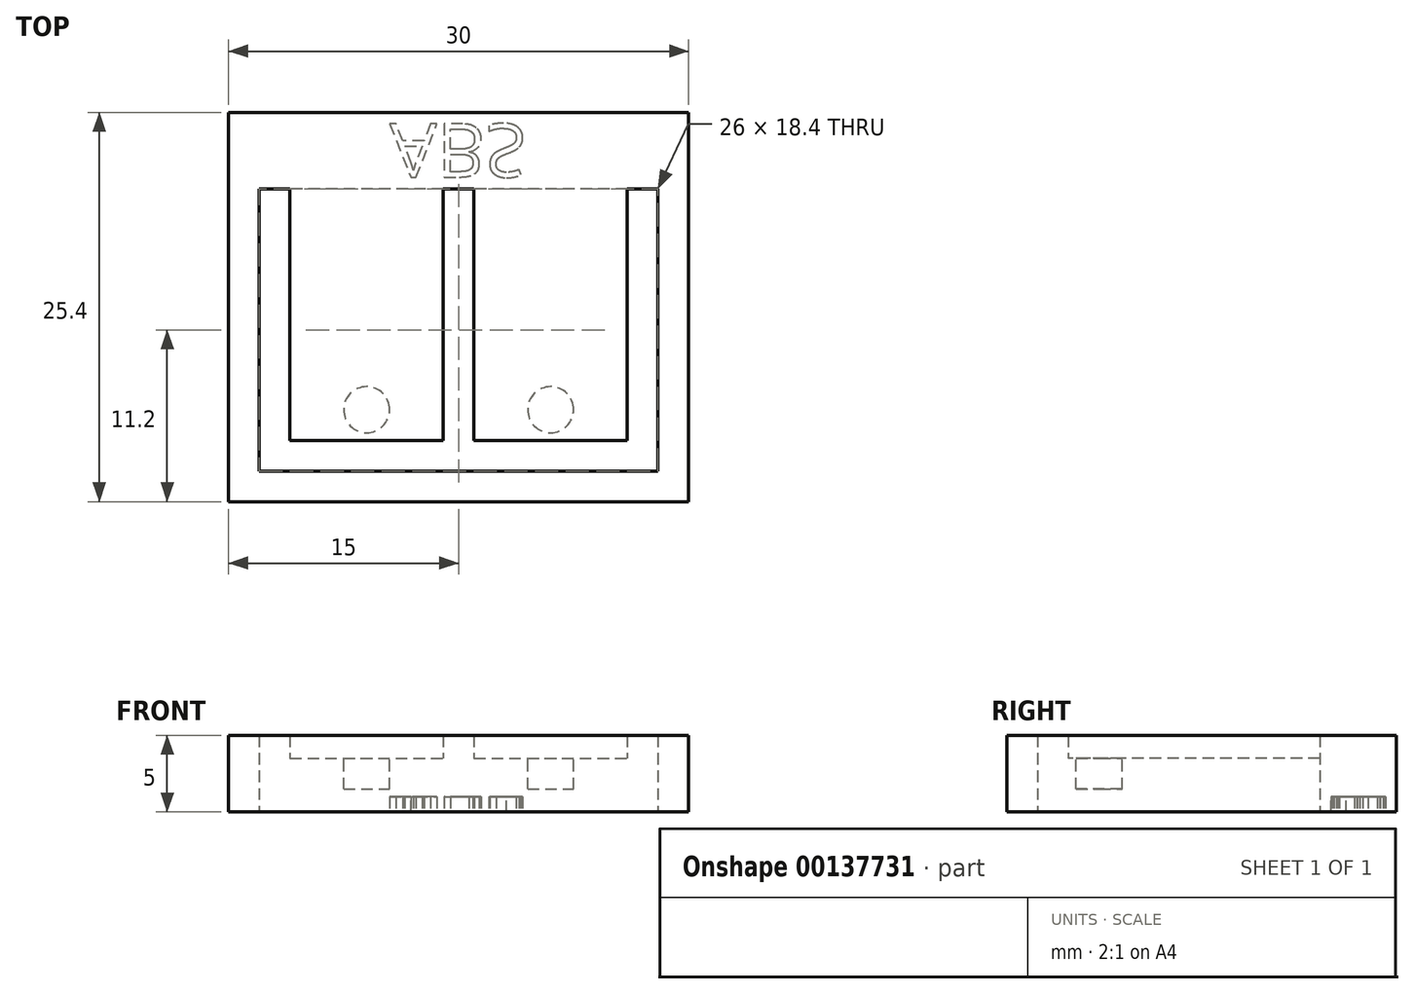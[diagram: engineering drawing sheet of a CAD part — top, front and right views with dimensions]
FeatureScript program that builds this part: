
annotation { "Feature Type Name" : "Feature", "Feature Type Description" : "" }
export const myFeature = defineFeature(function(context is Context, id is Id, definition is map)
    precondition{}
    {
        {
            var Q0;
            Q0=qCreatedBy(makeId("Top.planeOp"),FACE);
            var sketch = newSketch(context, id + "F0", { "sketchPlane" : qUnion([Q0])});
            skLineSegment(sketch, "E0.bottom", {"start": v(15, 12.7) * mm, "end": v(-15, 12.7) * mm});
            skLineSegment(sketch, "E0.top", {"start": v(15, -12.7) * mm, "end": v(-15, -12.7) * mm});
            skLineSegment(sketch, "E0.left", {"start": v(15, 12.7) * mm, "end": v(15, -12.7) * mm});
            skLineSegment(sketch, "E0.right", {"start": v(-15, 12.7) * mm, "end": v(-15, -12.7) * mm});
            skPoint(sketch, "E0.middle", {"position": v(0, 0) * mm});
            skLineSegment(sketch, "E1", {"start": v(-11, 7.7) * mm, "end": v(-11, -8.7) * mm});
            skLineSegment(sketch, "E2", {"start": v(-11, -8.7) * mm, "end": v(-1, -8.7) * mm});
            skLineSegment(sketch, "E3", {"start": v(-1, -8.7) * mm, "end": v(-1, 7.7) * mm});
            skLineSegment(sketch, "E4", {"start": v(-1, 7.7) * mm, "end": v(1, 7.7) * mm});
            skLineSegment(sketch, "E5", {"start": v(1, 7.7) * mm, "end": v(1, -8.7) * mm});
            skLineSegment(sketch, "E6", {"start": v(1, -8.7) * mm, "end": v(11, -8.7) * mm});
            skLineSegment(sketch, "E7", {"start": v(11, -8.7) * mm, "end": v(11, 7.7) * mm});
            skLineSegment(sketch, "E8", {"start": v(11, 7.7) * mm, "end": v(13, 7.7) * mm});
            skLineSegment(sketch, "E9", {"start": v(13, 7.7) * mm, "end": v(13, -10.7) * mm});
            skLineSegment(sketch, "E10", {"start": v(13, -10.7) * mm, "end": v(-13, -10.7) * mm});
            skLineSegment(sketch, "E11", {"start": v(-13, -10.7) * mm, "end": v(-13, 7.7) * mm});
            skLineSegment(sketch, "E12", {"start": v(-13, 7.7) * mm, "end": v(-11, 7.7) * mm});
            skSolve(sketch);
        }
        {
            var Q0;
            Q0=makeQuery(id+"F0.imprint","IMPRINT",FACE,{"disambiguationData":[TD([[makeQuery(id+"F0.imprint","IMPRINT",EDGE,{"derivedFrom":sQuery(id+"F0.wireOp",EDGE,"E0.bottom")}),1.0]])]});
            var Q1;
            Q1 = qConstructionFilter(qBodyType(qCreatedBy(id + "F0" ,EDGE), BodyType.WIRE), ConstructionObject.NO);
            extrude(context, id + "F1", {"entities" : qUnion([Q0]), "surfaceEntities" : qUnion([Q1]), "depth" : 5 * mm});
        }
        {
            var Q0;
            Q0=makeQuery(id+"F1.opExtrude","CAP_FACE",FACE,{"disambiguationData":[OSD([sQuery(id+"F0.wireOp",EDGE,"E0.bottom"),sQuery(id+"F0.wireOp",EDGE,"E0.top"),sQuery(id+"F0.wireOp",EDGE,"E0.left"),sQuery(id+"F0.wireOp",EDGE,"E0.right"),sQuery(id+"F0.wireOp",EDGE,"E1"),sQuery(id+"F0.wireOp",EDGE,"E2"),sQuery(id+"F0.wireOp",EDGE,"E3"),sQuery(id+"F0.wireOp",EDGE,"E4"),sQuery(id+"F0.wireOp",EDGE,"E5"),sQuery(id+"F0.wireOp",EDGE,"E6"),sQuery(id+"F0.wireOp",EDGE,"E7"),sQuery(id+"F0.wireOp",EDGE,"E8"),sQuery(id+"F0.wireOp",EDGE,"E9"),sQuery(id+"F0.wireOp",EDGE,"E10"),sQuery(id+"F0.wireOp",EDGE,"E11"),sQuery(id+"F0.wireOp",EDGE,"E12")])],"isStart":true});
            var sketch = newSketch(context, id + "F2", { "sketchPlane" : qUnion([Q0])});
            skLineSegment(sketch, "E13.0", {"start": v(-11, -7.7) * mm, "end": v(-11, 8.7) * mm});
            skLineSegment(sketch, "E13.1", {"start": v(11, 8.7) * mm, "end": v(11, -7.7) * mm});
            skLineSegment(sketch, "E14", {"start": v(-11, 8.7) * mm, "end": v(11, 8.7) * mm});
            skLineSegment(sketch, "E15", {"start": v(11, -7.7) * mm, "end": v(-11, -7.7) * mm});
            skSolve(sketch);
        }
        {
            var Q0;
            Q0 = qSketchRegion(id + "F2", true);
            extrude(context, id + "F3", {"entities" : qUnion([Q0]), "operationType" : NewBodyOperationType.REMOVE, "oppositeDirection" : true, "depth" : 3.5 * mm});
        }
        {
            var Q0;
            Q0=makeQuery(id+"F3.boolean.opBoolean","COPY",FACE,{"disambiguationData":[OD(1.0)],"derivedFrom":makeQuery(id+"F3.opExtrude","CAP_FACE",FACE,{"disambiguationData":[OSD([sQuery(id+"F2.wireOp",EDGE,"E13.0"),sQuery(id+"F2.wireOp",EDGE,"E13.1"),sQuery(id+"F2.wireOp",EDGE,"E14"),sQuery(id+"F2.wireOp",EDGE,"E15")])],"isStart":false})});
            var sketch = newSketch(context, id + "F4", { "sketchPlane" : qUnion([Q0])});
            skCircle(sketch, "E16", {"center": v(6, 6.7) * mm, "radius": 1.5 * mm});
            skPoint(sketch, "E16.centerSnap0", {"position": v(6, 8.7) * mm});
            skCircle(sketch, "E17.MirrorC", {"center": v(-6, 6.7) * mm, "radius": 1.5 * mm});
            skSolve(sketch);
        }
        {
            var Q0;
            Q0 = qSketchRegion(id + "F4", true);
            extrude(context, id + "F5", {"entities" : qUnion([Q0]), "operationType" : NewBodyOperationType.ADD, "depth" : 2 * mm});
        }
        {
            var Q0;
            Q0=makeQuery(id+"F1.opExtrude","CAP_FACE",FACE,{"disambiguationData":[OSD([sQuery(id+"F0.wireOp",EDGE,"E0.bottom"),sQuery(id+"F0.wireOp",EDGE,"E0.top"),sQuery(id+"F0.wireOp",EDGE,"E0.left"),sQuery(id+"F0.wireOp",EDGE,"E0.right"),sQuery(id+"F0.wireOp",EDGE,"E1"),sQuery(id+"F0.wireOp",EDGE,"E2"),sQuery(id+"F0.wireOp",EDGE,"E3"),sQuery(id+"F0.wireOp",EDGE,"E4"),sQuery(id+"F0.wireOp",EDGE,"E5"),sQuery(id+"F0.wireOp",EDGE,"E6"),sQuery(id+"F0.wireOp",EDGE,"E7"),sQuery(id+"F0.wireOp",EDGE,"E8"),sQuery(id+"F0.wireOp",EDGE,"E9"),sQuery(id+"F0.wireOp",EDGE,"E10"),sQuery(id+"F0.wireOp",EDGE,"E11"),sQuery(id+"F0.wireOp",EDGE,"E12")])],"isStart":true});
            var sketch = newSketch(context, id + "F6", { "sketchPlane" : qUnion([Q0])});
            skText(sketch, "E18", { "text": "ABS", "fontName": "OpenSans-Regular.ttf"});
            const initialGuessF6  = {"E18": [-0.00449, -0.01195, 1, 0, 0.0035]};
            skSetInitialGuess(sketch, initialGuessF6);
            skSolve(sketch);
        }
        {
            var Q0;
            Q0 = qSketchRegion(id + "F6", true);
            extrude(context, id + "F7", {"entities" : qUnion([Q0]), "operationType" : NewBodyOperationType.REMOVE, "oppositeDirection" : true, "depth" : 1 * mm});
        }
    });
